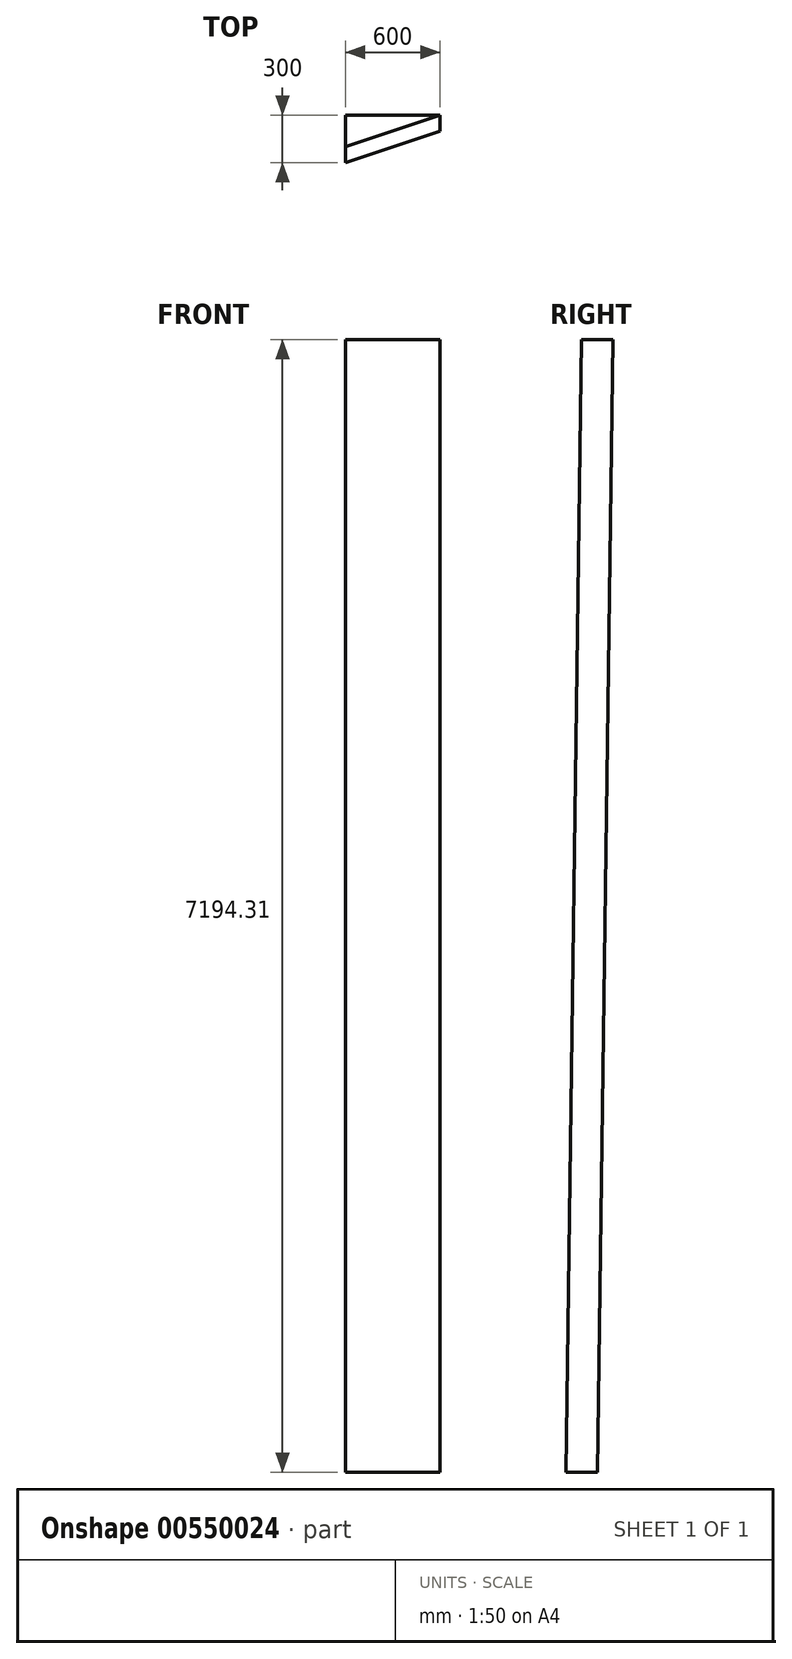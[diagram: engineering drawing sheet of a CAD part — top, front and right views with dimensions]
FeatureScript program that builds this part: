
annotation { "Feature Type Name" : "Feature", "Feature Type Description" : "" }
export const myFeature = defineFeature(function(context is Context, id is Id, definition is map)
    precondition{}
    {
        {
            var Q0;
            Q0=qCreatedBy(makeId("Top.planeOp"),FACE);
            var sketch = newSketch(context, id + "F0", { "sketchPlane" : qUnion([Q0])});
            skLineSegment(sketch, "E0", {"start": v(0, 0) * mm, "end": v(600, 0) * mm});
            skLineSegment(sketch, "E1", {"start": v(600, 0) * mm, "end": v(0, -200) * mm});
            skLineSegment(sketch, "E2", {"start": v(0, -200) * mm, "end": v(0, 0) * mm});
            skSolve(sketch);
        }
        {
            var Q0;
            Q0=qCreatedBy(makeId("Right.planeOp"),FACE);
            var sketch = newSketch(context, id + "F1", { "sketchPlane" : qUnion([Q0])});
            skLineSegment(sketch, "E3.0", {"start": v(-200, 0) * mm, "end": v(0, 0) * mm});
            skLineSegment(sketch, "E4", {"start": v(0, 0) * mm, "end": v(-100, -7194.3) * mm});
            skSolve(sketch);
        }
        {
            var Q0;
            Q0=makeQuery(id+"F0.imprint","IMPRINT",FACE,{"disambiguationData":[TD([[makeQuery(id+"F0.imprint","IMPRINT",EDGE,{"derivedFrom":sQuery(id+"F0.wireOp",EDGE,"E0")}),-1.0]])]});
            var Q1;
            Q1=sQuery(id+"F1.wireOp",EDGE,"E4");
            sweep(context, id + "F2", {"profiles" : qUnion([Q0]), "path" : qUnion([Q1])});
        }
    });
